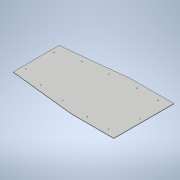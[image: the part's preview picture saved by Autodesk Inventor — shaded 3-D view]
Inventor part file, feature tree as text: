
AUTODESK INVENTOR PART (.ipt)
format: ipt  version: 2021 (Build 250183000, 183)  size: 138,752 bytes
history: native  units: in
note: dims shown in document units (in); Inventor stores cm internally (conversion verified against a paired STEP export)
features: sketch x1, extrude x1, hole x1
ambient origin geometry x8: Origin, YZ Plane, XZ Plane, XY Plane, X Axis, Y Axis, Z Axis, Center Point
bodies: Solid1 (feature_tree)
feature tree (3):
  sketch  "Sketch1"  dims[d0=8.5in d1=12.0in d2=30.5in d3=8.5in d4=12.0in d5=6.5in d6=6.5in d7=0.125in d8=0.0in d9=3.0in d10=1.5in d11=3.0in d12=1.5in d15=4.0in d16=1.0in d17=4.0in d18=1.0in d23=3.0in d24=1.5in d25=3.0in d26=1.5in d32=1.0in d34=7.0in d35=1.5in d36=7.0in d37=1.5in d38=7.0in d39=1.5in d40=7.0in d41=1.5in d42=0.201in d43=0.75in d44=0.385in d45=0.25in d46=0.5635in d47=1.0in d48=0.8108in]
  extrude  "Extrusion1"  Depth=0.125in
  hole  "Hole1"  [1 undecoded]
note: 1 required parameter value undecoded (feature->parameter linkage not recoverable at this tier; creation-order binding heuristic only, values carry confidence <= 0.55)
